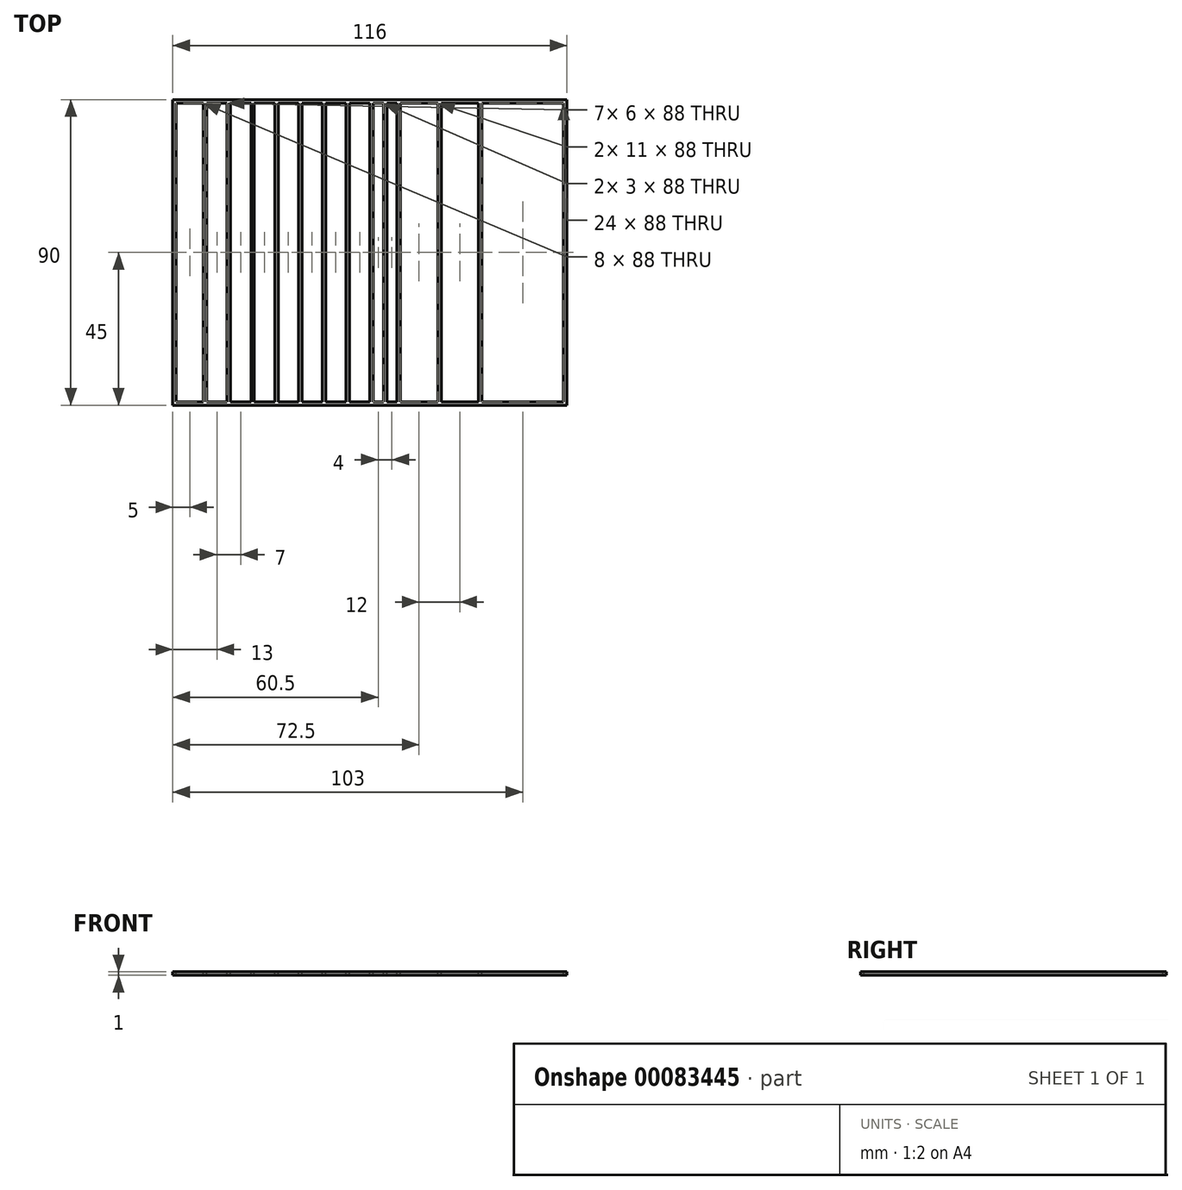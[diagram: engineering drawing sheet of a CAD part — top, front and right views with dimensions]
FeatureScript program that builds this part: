
annotation { "Feature Type Name" : "Feature", "Feature Type Description" : "" }
export const myFeature = defineFeature(function(context is Context, id is Id, definition is map)
    precondition{}
    {
        {
            assignVariable(context, id + "F0", {"name" : "holderHeight", "anyValue" : 1});
        }
        {
            var Q0;
            Q0=qCreatedBy(makeId("Top.planeOp"),FACE);
            var sketch = newSketch(context, id + "F1", { "sketchPlane" : qUnion([Q0])});
            skLineSegment(sketch, "E0.bottom", {"start": v(-58, -45) * mm, "end": v(58, -45) * mm});
            skLineSegment(sketch, "E0.top", {"start": v(-58, 45) * mm, "end": v(58, 45) * mm});
            skLineSegment(sketch, "E0.left", {"start": v(-58, -45) * mm, "end": v(-58, 45) * mm});
            skLineSegment(sketch, "E0.right", {"start": v(58, -45) * mm, "end": v(58, 45) * mm});
            skSolve(sketch);
        }
        {
            var Q0;
            Q0=makeQuery(id+"F1.imprint","IMPRINT",FACE,{"disambiguationData":[TD([[makeQuery(id+"F1.imprint","IMPRINT",EDGE,{"derivedFrom":sQuery(id+"F1.wireOp",EDGE,"E0.bottom")}),1.0]])]});
            extrude(context, id + "F2", {"entities" : qUnion([Q0]), "depth" : getVariable(context, 'holderHeight') * mm});
        }
        {
            var Q0;
            Q0=makeQuery(id+"F2.opExtrude","CAP_FACE",FACE,{"disambiguationData":[OSD([sQuery(id+"F1.wireOp",EDGE,"E0.bottom"),sQuery(id+"F1.wireOp",EDGE,"E0.top"),sQuery(id+"F1.wireOp",EDGE,"E0.left"),sQuery(id+"F1.wireOp",EDGE,"E0.right")])],"isStart":false});
            var sketch = newSketch(context, id + "F3", { "sketchPlane" : qUnion([Q0])});
            skPoint(sketch, "E1.middle", {"position": v(0, 0) * mm});
            skLineSegment(sketch, "E2.bottom", {"start": v(-49, 44) * mm, "end": v(-57, 44) * mm});
            skLineSegment(sketch, "E2.top", {"start": v(-49, -44) * mm, "end": v(-57, -44) * mm});
            skLineSegment(sketch, "E2.left", {"start": v(-49, 44) * mm, "end": v(-49, -44) * mm});
            skLineSegment(sketch, "E2.right", {"start": v(-57, 44) * mm, "end": v(-57, -44) * mm});
            skPoint(sketch, "E2.middle", {"position": v(-53, 0) * mm});
            skLineSegment(sketch, "E3", {"start": v(0, 0) * mm, "end": v(-109.38, 0) * mm, "construction": true});
            skLineSegment(sketch, "E4.bottom", {"start": v(-42, 44) * mm, "end": v(-48, 44) * mm});
            skLineSegment(sketch, "E4.top", {"start": v(-42, -44) * mm, "end": v(-48, -44) * mm});
            skLineSegment(sketch, "E4.left", {"start": v(-42, 44) * mm, "end": v(-42, -44) * mm});
            skLineSegment(sketch, "E4.right", {"start": v(-48, 44) * mm, "end": v(-48, -44) * mm});
            skPoint(sketch, "E4.middle", {"position": v(-45, 0) * mm});
            skPoint(sketch, "E4.cornerSnap0", {"position": v(-53, 44) * mm});
            skLineSegment(sketch, "E5.1.0.0", {"start": v(-35, 44) * mm, "end": v(-35, -44) * mm});
            skLineSegment(sketch, "E5.1.0.1", {"start": v(-35, 44) * mm, "end": v(-41, 44) * mm});
            skLineSegment(sketch, "E5.1.0.2", {"start": v(-41, 44) * mm, "end": v(-41, -44) * mm});
            skLineSegment(sketch, "E5.1.0.3", {"start": v(-35, -44) * mm, "end": v(-41, -44) * mm});
            skLineSegment(sketch, "E5.2.0.0", {"start": v(-28, 44) * mm, "end": v(-28, -44) * mm});
            skLineSegment(sketch, "E5.2.0.1", {"start": v(-28, 44) * mm, "end": v(-34, 44) * mm});
            skLineSegment(sketch, "E5.2.0.2", {"start": v(-34, 44) * mm, "end": v(-34, -44) * mm});
            skLineSegment(sketch, "E5.2.0.3", {"start": v(-28, -44) * mm, "end": v(-34, -44) * mm});
            skLineSegment(sketch, "E5.3.0.0", {"start": v(-21, 44) * mm, "end": v(-21, -44) * mm});
            skLineSegment(sketch, "E5.3.0.1", {"start": v(-21, 44) * mm, "end": v(-27, 44) * mm});
            skLineSegment(sketch, "E5.3.0.2", {"start": v(-27, 44) * mm, "end": v(-27, -44) * mm});
            skLineSegment(sketch, "E5.3.0.3", {"start": v(-21, -44) * mm, "end": v(-27, -44) * mm});
            skLineSegment(sketch, "E5.4.0.0", {"start": v(-14, 44) * mm, "end": v(-14, -44) * mm});
            skLineSegment(sketch, "E5.4.0.1", {"start": v(-14, 44) * mm, "end": v(-20, 44) * mm});
            skLineSegment(sketch, "E5.4.0.2", {"start": v(-20, 44) * mm, "end": v(-20, -44) * mm});
            skLineSegment(sketch, "E5.4.0.3", {"start": v(-14, -44) * mm, "end": v(-20, -44) * mm});
            skLineSegment(sketch, "E5.5.0.0", {"start": v(-7, 44) * mm, "end": v(-7, -44) * mm});
            skLineSegment(sketch, "E5.5.0.1", {"start": v(-7, 44) * mm, "end": v(-13, 44) * mm});
            skLineSegment(sketch, "E5.5.0.2", {"start": v(-13, 44) * mm, "end": v(-13, -44) * mm});
            skLineSegment(sketch, "E5.5.0.3", {"start": v(-7, -44) * mm, "end": v(-13, -44) * mm});
            skLineSegment(sketch, "E5.direction1", {"start": v(-42, -44) * mm, "end": v(-35, -44) * mm, "construction": true});
            skLineSegment(sketch, "E6.0.6.0", {"start": v(0, 44) * mm, "end": v(0, -44) * mm});
            skLineSegment(sketch, "E6.3.6.0", {"start": v(0, 44) * mm, "end": v(-6, 44) * mm});
            skLineSegment(sketch, "E6.6.6.0", {"start": v(-6, 44) * mm, "end": v(-6, -44) * mm});
            skLineSegment(sketch, "E6.9.6.0", {"start": v(0, -44) * mm, "end": v(-6, -44) * mm});
            skLineSegment(sketch, "E7", {"start": v(0, 0) * mm, "end": v(83.05, 0) * mm, "construction": true});
            skLineSegment(sketch, "E8.bottom", {"start": v(1, -44) * mm, "end": v(4, -44) * mm});
            skLineSegment(sketch, "E8.top", {"start": v(1, 44) * mm, "end": v(4, 44) * mm});
            skLineSegment(sketch, "E8.left", {"start": v(1, -44) * mm, "end": v(1, 44) * mm});
            skLineSegment(sketch, "E8.right", {"start": v(4, -44) * mm, "end": v(4, 44) * mm});
            skPoint(sketch, "E8.middle", {"position": v(2.5, 0) * mm});
            skLineSegment(sketch, "E9.bottom", {"start": v(5, -44) * mm, "end": v(8, -44) * mm});
            skLineSegment(sketch, "E9.top", {"start": v(5, 44) * mm, "end": v(8, 44) * mm});
            skLineSegment(sketch, "E9.left", {"start": v(5, -44) * mm, "end": v(5, 44) * mm});
            skLineSegment(sketch, "E9.right", {"start": v(8, -44) * mm, "end": v(8, 44) * mm});
            skPoint(sketch, "E9.middle", {"position": v(6.5, 0) * mm});
            skLineSegment(sketch, "E10.bottom", {"start": v(9, -44) * mm, "end": v(20, -44) * mm});
            skLineSegment(sketch, "E10.top", {"start": v(9, 44) * mm, "end": v(20, 44) * mm});
            skLineSegment(sketch, "E10.left", {"start": v(9, -44) * mm, "end": v(9, 44) * mm});
            skLineSegment(sketch, "E10.right", {"start": v(20, -44) * mm, "end": v(20, 44) * mm});
            skPoint(sketch, "E10.middle", {"position": v(14.5, 0) * mm});
            skLineSegment(sketch, "E11.1.0.0", {"start": v(32, -44) * mm, "end": v(32, 44) * mm});
            skLineSegment(sketch, "E11.1.0.1", {"start": v(21, 44) * mm, "end": v(32, 44) * mm});
            skLineSegment(sketch, "E11.1.0.2", {"start": v(21, -44) * mm, "end": v(21, 44) * mm});
            skLineSegment(sketch, "E11.1.0.3", {"start": v(21, -44) * mm, "end": v(32, -44) * mm});
            skLineSegment(sketch, "E11.direction1", {"start": v(20, -44) * mm, "end": v(32, -44) * mm, "construction": true});
            skLineSegment(sketch, "E12.bottom", {"start": v(33, -44) * mm, "end": v(57, -44) * mm});
            skLineSegment(sketch, "E12.top", {"start": v(33, 44) * mm, "end": v(57, 44) * mm});
            skLineSegment(sketch, "E12.left", {"start": v(33, -44) * mm, "end": v(33, 44) * mm});
            skLineSegment(sketch, "E12.right", {"start": v(57, -44) * mm, "end": v(57, 44) * mm});
            skPoint(sketch, "E12.middle", {"position": v(45, 0) * mm});
            skSolve(sketch);
        }
        {
            var Q0;
            Q0=makeQuery(id+"F2.opExtrude","CAP_FACE",FACE,{"disambiguationData":[OSD([sQuery(id+"F1.wireOp",EDGE,"E0.bottom"),sQuery(id+"F1.wireOp",EDGE,"E0.top"),sQuery(id+"F1.wireOp",EDGE,"E0.left"),sQuery(id+"F1.wireOp",EDGE,"E0.right")])],"isStart":false});
            var sketch = newSketch(context, id + "F4", { "sketchPlane" : qUnion([Q0])});
            skLineSegment(sketch, "E13.bottom", {"start": v(-58, -29.33) * mm, "end": v(58, -29.33) * mm});
            skLineSegment(sketch, "E13.top", {"start": v(-58, 29.33) * mm, "end": v(58, 29.33) * mm});
            skLineSegment(sketch, "E13.left", {"start": v(-58, -29.33) * mm, "end": v(-58, 29.33) * mm});
            skLineSegment(sketch, "E13.right", {"start": v(58, -29.33) * mm, "end": v(58, 29.33) * mm});
            skPoint(sketch, "E13.middle", {"position": v(0, 0) * mm});
            skSolve(sketch);
        }
        {
            var Q0;
            Q0=qSketchRegion(id+"F4",true);
            extrude(context, id + "F5", {"entities" : qUnion([Q0]), "operationType" : NewBodyOperationType.REMOVE, "oppositeDirection" : true, "depth" : (getVariable(context, 'holderHeight') - 4) * mm});
        }
        {
            var Q0;
            Q0=makeQuery(id+"F3.imprint","IMPRINT",FACE,{"disambiguationData":[TD([[makeQuery(id+"F3.imprint","IMPRINT",EDGE,{"derivedFrom":sQuery(id+"F3.wireOp",EDGE,"E2.bottom")}),1.0]])]});
            var Q1;
            Q1=makeQuery(id+"F3.imprint","IMPRINT",FACE,{"disambiguationData":[TD([[makeQuery(id+"F3.imprint","IMPRINT",EDGE,{"derivedFrom":sQuery(id+"F3.wireOp",EDGE,"E4.bottom")}),1.0]])]});
            var Q2;
            Q2=makeQuery(id+"F3.imprint","IMPRINT",FACE,{"disambiguationData":[TD([[makeQuery(id+"F3.imprint","IMPRINT",EDGE,{"derivedFrom":sQuery(id+"F3.wireOp",EDGE,"E5.1.0.0")}),-1.0]])]});
            var Q3;
            Q3=makeQuery(id+"F3.imprint","IMPRINT",FACE,{"disambiguationData":[TD([[makeQuery(id+"F3.imprint","IMPRINT",EDGE,{"derivedFrom":sQuery(id+"F3.wireOp",EDGE,"E5.2.0.0")}),-1.0]])]});
            var Q4;
            Q4=makeQuery(id+"F3.imprint","IMPRINT",FACE,{"disambiguationData":[TD([[makeQuery(id+"F3.imprint","IMPRINT",EDGE,{"derivedFrom":sQuery(id+"F3.wireOp",EDGE,"E5.3.0.0")}),-1.0]])]});
            var Q5;
            Q5=makeQuery(id+"F3.imprint","IMPRINT",FACE,{"disambiguationData":[TD([[makeQuery(id+"F3.imprint","IMPRINT",EDGE,{"derivedFrom":sQuery(id+"F3.wireOp",EDGE,"E5.4.0.0")}),-1.0]])]});
            var Q6;
            Q6=makeQuery(id+"F3.imprint","IMPRINT",FACE,{"disambiguationData":[TD([[makeQuery(id+"F3.imprint","IMPRINT",EDGE,{"derivedFrom":sQuery(id+"F3.wireOp",EDGE,"E5.5.0.0")}),-1.0]])]});
            var Q7;
            Q7=makeQuery(id+"F3.imprint","IMPRINT",FACE,{"disambiguationData":[TD([[makeQuery(id+"F3.imprint","IMPRINT",EDGE,{"derivedFrom":sQuery(id+"F3.wireOp",EDGE,"E6.0.6.0")}),-1.0]])]});
            var Q8;
            Q8=makeQuery(id+"F3.imprint","IMPRINT",FACE,{"disambiguationData":[TD([[makeQuery(id+"F3.imprint","IMPRINT",EDGE,{"derivedFrom":sQuery(id+"F3.wireOp",EDGE,"E8.bottom")}),1.0]])]});
            var Q9;
            Q9=makeQuery(id+"F3.imprint","IMPRINT",FACE,{"disambiguationData":[TD([[makeQuery(id+"F3.imprint","IMPRINT",EDGE,{"derivedFrom":sQuery(id+"F3.wireOp",EDGE,"E9.bottom")}),1.0]])]});
            var Q10;
            Q10=makeQuery(id+"F3.imprint","IMPRINT",FACE,{"disambiguationData":[TD([[makeQuery(id+"F3.imprint","IMPRINT",EDGE,{"derivedFrom":sQuery(id+"F3.wireOp",EDGE,"E10.bottom")}),1.0]])]});
            var Q11;
            Q11=makeQuery(id+"F3.imprint","IMPRINT",FACE,{"disambiguationData":[TD([[makeQuery(id+"F3.imprint","IMPRINT",EDGE,{"derivedFrom":sQuery(id+"F3.wireOp",EDGE,"E11.1.0.0")}),1.0]])]});
            var Q12;
            Q12=makeQuery(id+"F3.imprint","IMPRINT",FACE,{"disambiguationData":[TD([[makeQuery(id+"F3.imprint","IMPRINT",EDGE,{"derivedFrom":sQuery(id+"F3.wireOp",EDGE,"E12.bottom")}),1.0]])]});
            extrude(context, id + "F6", {"entities" : qUnion([Q0, Q1, Q2, Q3, Q4, Q5, Q6, Q7, Q8, Q9, Q10, Q11, Q12]), "operationType" : NewBodyOperationType.REMOVE, "oppositeDirection" : true, "depth" : 1 * mm});
        }
    });
